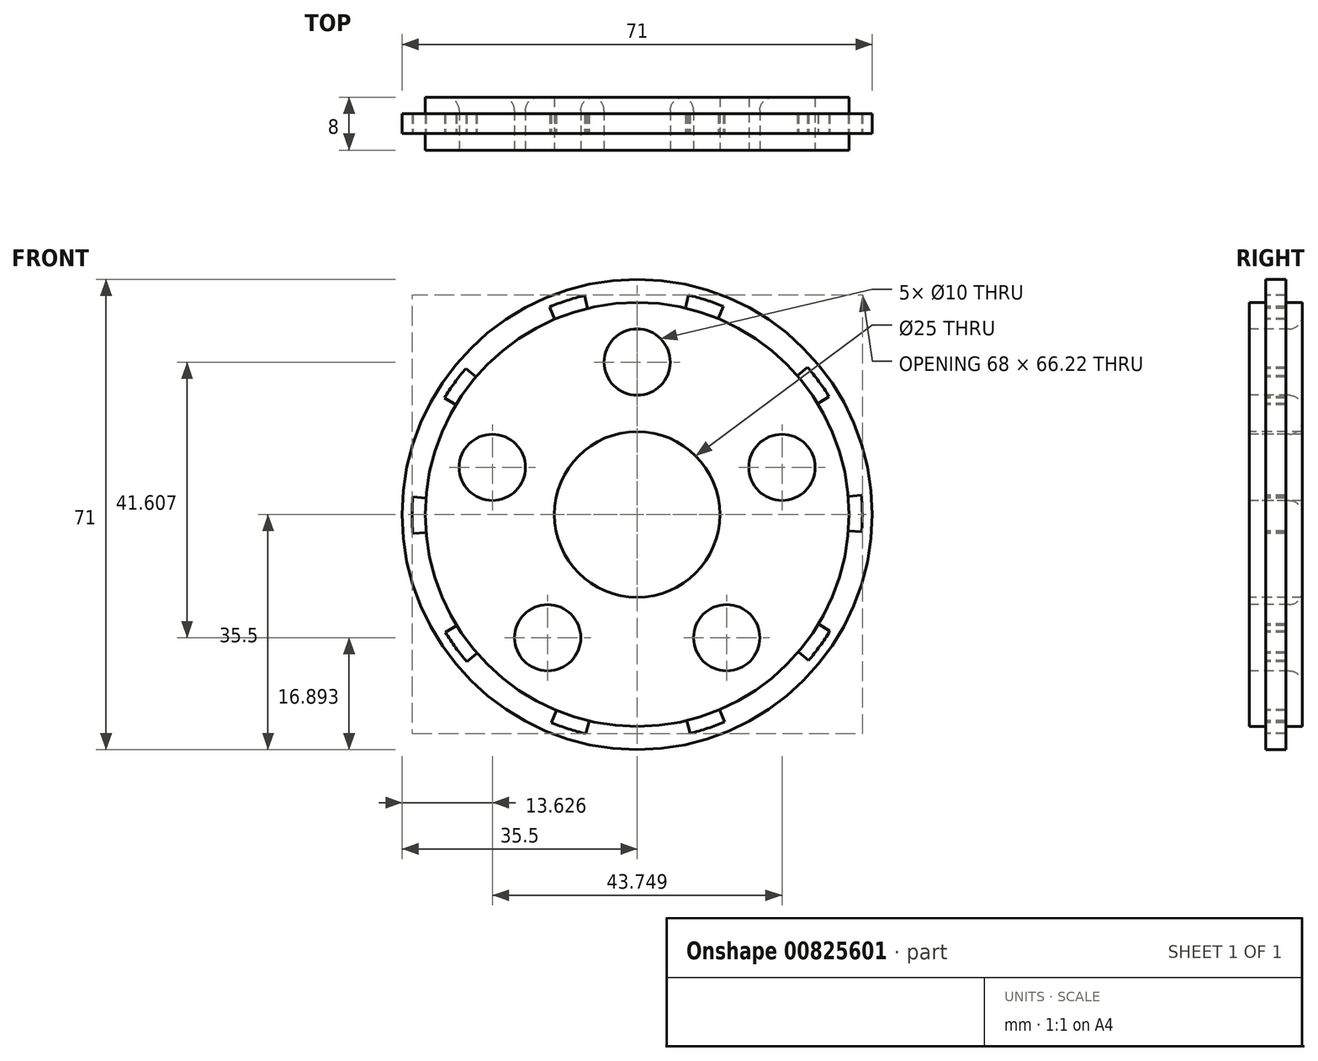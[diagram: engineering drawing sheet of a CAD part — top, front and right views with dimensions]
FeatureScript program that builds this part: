
annotation { "Feature Type Name" : "Feature", "Feature Type Description" : "" }
export const myFeature = defineFeature(function(context is Context, id is Id, definition is map)
    precondition{}
    {
        {
            var Q0;
            Q0=qCreatedBy(makeId("Front.planeOp"),FACE);
            var sketch = newSketch(context, id + "F0", { "sketchPlane" : qUnion([Q0])});
            skCircle(sketch, "E0", {"center": v(0, 0) * mm, "radius": 35.5 * mm});
            skSolve(sketch);
        }
        {
            var Q0;
            Q0=qSketchRegion(id+"F0",true);
            extrude(context, id + "F1", {"entities" : qUnion([Q0]), "oppositeDirection" : true, "depth" : 4 * mm, "hasSecondDirection" : true, "secondDirectionOppositeDirection" : false, "secondDirectionDepth" : 4 * mm, "offsetDistance" : 25 * mm});
        }
        {
            var Q0;
            Q0=makeQuery(id+"F1.opExtrude","CAP_FACE",FACE,{"disambiguationData":[OSD([sQuery(id+"F0.wireOp",EDGE,"E0")])],"isStart":true});
            var sketch = newSketch(context, id + "F2", { "sketchPlane" : qUnion([Q0])});
            skCircle(sketch, "E1", {"center": v(0, 0) * mm, "radius": 12.5 * mm});
            skSolve(sketch);
        }
        {
            var Q0;
            Q0=qSketchRegion(id+"F2",true);
            extrude(context, id + "F3", {"entities" : qUnion([Q0]), "operationType" : NewBodyOperationType.REMOVE, "oppositeDirection" : true, "depth" : 25 * mm});
        }
        {
            var Q0;
            Q0=makeQuery(id+"F1.opExtrude","CAP_FACE",FACE,{"disambiguationData":[OSD([sQuery(id+"F0.wireOp",EDGE,"E0")])],"isStart":true});
            var sketch = newSketch(context, id + "F4", { "sketchPlane" : qUnion([Q0])});
            skCircle(sketch, "E2", {"center": v(0, 23) * mm, "radius": 5 * mm});
            skLineSegment(sketch, "E3", {"start": v(0, 31) * mm, "end": v(0, 15) * mm, "construction": true});
            skCircle(sketch, "E4.1.0", {"center": v(-21.87, 7.1) * mm, "radius": 5 * mm});
            skCircle(sketch, "E4.2.0", {"center": v(-13.52, -18.6) * mm, "radius": 5 * mm});
            skPoint(sketch, "E4.center", {"position": v(0, 0) * mm});
            skCircle(sketch, "E5", {"center": v(0, 0) * mm, "radius": 15 * mm, "construction": true});
            skCircle(sketch, "E6", {"center": v(0, 0) * mm, "radius": 31 * mm, "construction": true});
            skCircle(sketch, "E7.1.3.0", {"center": v(13.52, -18.6) * mm, "radius": 5 * mm});
            skCircle(sketch, "E8.1.4.0", {"center": v(21.87, 7.1) * mm, "radius": 5 * mm});
            skSolve(sketch);
        }
        {
            var Q0;
            Q0=qSketchRegion(id+"F4",true);
            extrude(context, id + "F5", {"entities" : qUnion([Q0]), "operationType" : NewBodyOperationType.REMOVE, "oppositeDirection" : true, "depth" : 25 * mm});
        }
        {
            var Q0;
            Q0=makeQuery(id+"F1.opExtrude","CAP_FACE",FACE,{"disambiguationData":[OSD([sQuery(id+"F0.wireOp",EDGE,"E0")])],"isStart":true});
            var sketch = newSketch(context, id + "F6", { "sketchPlane" : qUnion([Q0])});
            skCircle(sketch, "E9", {"center": v(0, 0) * mm, "radius": 15 * mm, "construction": true});
            skSolve(sketch);
        }
        {
            var Q0;
            Q0=makeQuery(id+"F5.boolean.opBoolean","COPY",EDGE,{"derivedFrom":makeQuery(id+"F5.opExtrude","CAP_EDGE",EDGE,{"disambiguationData":[OSD([sQuery(id+"F4.wireOp",EDGE,"E2")])],"isStart":true})});
            var Q1;
            Q1=makeQuery(id+"F5.boolean.opBoolean","COPY",EDGE,{"derivedFrom":makeQuery(id+"F5.opExtrude","CAP_EDGE",EDGE,{"disambiguationData":[OSD([sQuery(id+"F4.wireOp",EDGE,"E4.1.0")])],"isStart":true})});
            var Q2;
            Q2=makeQuery(id+"F5.boolean.opBoolean","COPY",EDGE,{"derivedFrom":makeQuery(id+"F5.opExtrude","CAP_EDGE",EDGE,{"disambiguationData":[OSD([sQuery(id+"F4.wireOp",EDGE,"E4.2.0")])],"isStart":true})});
            var Q3;
            Q3=makeQuery(id+"F5.boolean.opBoolean","INTERSECT",EDGE,{"derivedFrom":[makeQuery(id+"F1.opExtrude","CAP_FACE",FACE,{"disambiguationData":[OSD([sQuery(id+"F0.wireOp",EDGE,"E0")])],"isStart":false}),makeQuery(id+"F5.opExtrude","SWEPT_FACE",FACE,{"disambiguationData":[OSD([sQuery(id+"F4.wireOp",EDGE,"E4.1.0")])]})]});
            var Q4;
            Q4=makeQuery(id+"F5.boolean.opBoolean","INTERSECT",EDGE,{"derivedFrom":[makeQuery(id+"F1.opExtrude","CAP_FACE",FACE,{"disambiguationData":[OSD([sQuery(id+"F0.wireOp",EDGE,"E0")])],"isStart":false}),makeQuery(id+"F5.opExtrude","SWEPT_FACE",FACE,{"disambiguationData":[OSD([sQuery(id+"F4.wireOp",EDGE,"E4.2.0")])]})]});
            var Q5;
            Q5=makeQuery(id+"F5.boolean.opBoolean","INTERSECT",EDGE,{"derivedFrom":[makeQuery(id+"F1.opExtrude","CAP_FACE",FACE,{"disambiguationData":[OSD([sQuery(id+"F0.wireOp",EDGE,"E0")])],"isStart":false}),makeQuery(id+"F5.opExtrude","SWEPT_FACE",FACE,{"disambiguationData":[OSD([sQuery(id+"F4.wireOp",EDGE,"E2")])]})]});
            var Q6;
            Q6=makeQuery(id+"F5.boolean.opBoolean","COPY",EDGE,{"derivedFrom":makeQuery(id+"F5.opExtrude","CAP_EDGE",EDGE,{"disambiguationData":[OSD([sQuery(id+"F4.wireOp",EDGE,"a81bae41-d5ea-4544-bfaf-6c99a52da0b9.1.5.0")])],"isStart":true})});
            var Q7;
            Q7=makeQuery(id+"F5.boolean.opBoolean","COPY",EDGE,{"derivedFrom":makeQuery(id+"F5.opExtrude","CAP_EDGE",EDGE,{"disambiguationData":[OSD([sQuery(id+"F4.wireOp",EDGE,"E7.1.4.0")])],"isStart":true})});
            var Q8;
            Q8=makeQuery(id+"F5.boolean.opBoolean","COPY",EDGE,{"derivedFrom":makeQuery(id+"F5.opExtrude","CAP_EDGE",EDGE,{"disambiguationData":[OSD([sQuery(id+"F4.wireOp",EDGE,"E7.1.3.0")])],"isStart":true})});
            var Q9;
            Q9=makeQuery(id+"F5.boolean.opBoolean","INTERSECT",EDGE,{"derivedFrom":[makeQuery(id+"F1.opExtrude","CAP_FACE",FACE,{"disambiguationData":[OSD([sQuery(id+"F0.wireOp",EDGE,"E0")])],"isStart":false}),makeQuery(id+"F5.opExtrude","SWEPT_FACE",FACE,{"disambiguationData":[OSD([sQuery(id+"F4.wireOp",EDGE,"E7.1.3.0")])]})]});
            var Q10;
            Q10=makeQuery(id+"F5.boolean.opBoolean","INTERSECT",EDGE,{"derivedFrom":[makeQuery(id+"F1.opExtrude","CAP_FACE",FACE,{"disambiguationData":[OSD([sQuery(id+"F0.wireOp",EDGE,"E0")])],"isStart":false}),makeQuery(id+"F5.opExtrude","SWEPT_FACE",FACE,{"disambiguationData":[OSD([sQuery(id+"F4.wireOp",EDGE,"E7.1.4.0")])]})]});
            var Q11;
            Q11=makeQuery(id+"F5.boolean.opBoolean","INTERSECT",EDGE,{"derivedFrom":[makeQuery(id+"F1.opExtrude","CAP_FACE",FACE,{"disambiguationData":[OSD([sQuery(id+"F0.wireOp",EDGE,"E0")])],"isStart":false}),makeQuery(id+"F5.opExtrude","SWEPT_FACE",FACE,{"disambiguationData":[OSD([sQuery(id+"F4.wireOp",EDGE,"a81bae41-d5ea-4544-bfaf-6c99a52da0b9.1.5.0")])]})]});
            var Q12;
            Q12=makeQuery(id+"F5.boolean.opBoolean","COPY",EDGE,{"derivedFrom":makeQuery(id+"F5.opExtrude","CAP_EDGE",EDGE,{"disambiguationData":[OSD([sQuery(id+"F4.wireOp",EDGE,"E8.1.4.0")])],"isStart":true})});
            fillet(context, id + "F7", {"entities" : qUnion([Q0, Q1, Q2, Q3, Q4, Q5, Q6, Q7, Q8, Q9, Q10, Q11, Q12]), "radius" : 2 * mm, "tangentPropagation" : true, "allowEdgeOverflow" : false});
        }
        {
            var Q0;
            Q0=makeQuery(id+"F6.imprint","IMPRINT",FACE,{"disambiguationData":[TD([[makeQuery(id+"F6.imprint","IMPRINT",EDGE,{"derivedFrom":makeQuery(id+"F1.opExtrude","CAP_EDGE",EDGE,{"disambiguationData":[OSD([sQuery(id+"F0.wireOp",EDGE,"E0")])],"isStart":true})}),1.0]])]});
            var sketch = newSketch(context, id + "F8", { "sketchPlane" : qUnion([Q0])});
            skCircle(sketch, "E10", {"center": v(0, 0) * mm, "radius": 32 * mm});
            skCircle(sketch, "E11", {"center": v(0, 0) * mm, "radius": 36.35 * mm});
            skSolve(sketch);
        }
        {
            var Q0;
            Q0=qSketchRegion(id+"F8",true);
            extrude(context, id + "F9", {"entities" : qUnion([Q0]), "operationType" : NewBodyOperationType.REMOVE, "oppositeDirection" : true, "depth" : 2.5 * mm, "offsetDistance" : 25 * mm});
        }
        {
            var Q0;
            Q0=makeQuery(id+"F1.opExtrude","CAP_FACE",FACE,{"disambiguationData":[OSD([sQuery(id+"F0.wireOp",EDGE,"E0")])],"isStart":false});
            var sketch = newSketch(context, id + "F10", { "sketchPlane" : qUnion([Q0])});
            skCircle(sketch, "E12", {"center": v(0, 0) * mm, "radius": 32 * mm});
            skCircle(sketch, "E13", {"center": v(0, 0) * mm, "radius": 42.23 * mm});
            skSolve(sketch);
        }
        {
            var Q0;
            Q0=qSketchRegion(id+"F10",true);
            extrude(context, id + "F11", {"entities" : qUnion([Q0]), "operationType" : NewBodyOperationType.REMOVE, "oppositeDirection" : true, "depth" : 2.5 * mm, "offsetDistance" : 25 * mm});
        }
        {
            var Q0;
            Q0=makeQuery(id+"F9.boolean.opBoolean","COPY",FACE,{"derivedFrom":makeQuery(id+"F9.opExtrude","CAP_FACE",FACE,{"disambiguationData":[OSD([sQuery(id+"F8.wireOp",EDGE,"E10"),sQuery(id+"F8.wireOp",EDGE,"E11")])],"isStart":false})});
            var sketch = newSketch(context, id + "F12", { "sketchPlane" : qUnion([Q0])});
            skLineSegment(sketch, "E14", {"start": v(0, 33) * mm, "end": v(0, 0) * mm, "construction": true});
            skPoint(sketch, "E15.center", {"position": v(0, 0) * mm});
            skLineSegment(sketch, "E16", {"start": v(0, 0) * mm, "end": v(10.2, 31.38) * mm, "construction": true});
            skArc(sketch, "E17", {"start": v(12.22, 29.58) * mm, "mid": v(9.78, 30.47) * mm, "end": v(7.27, 31.16) * mm});
            skLineSegment(sketch, "E18", {"start": v(7.27, 31.16) * mm, "end": v(0, 0) * mm, "construction": true});
            skLineSegment(sketch, "E19", {"start": v(0, 0) * mm, "end": v(12.22, 29.58) * mm, "construction": true});
            skLineSegment(sketch, "E20", {"start": v(7.27, 31.16) * mm, "end": v(7.73, 33.11) * mm});
            skLineSegment(sketch, "E21", {"start": v(12.22, 29.58) * mm, "end": v(12.98, 31.42) * mm});
            skArc(sketch, "E22", {"start": v(12.98, 31.42) * mm, "mid": v(10.39, 32.37) * mm, "end": v(7.73, 33.11) * mm});
            skArc(sketch, "E23.1.0", {"start": v(-7.97, 33.05) * mm, "mid": v(-10.63, 32.3) * mm, "end": v(-13.21, 31.33) * mm});
            skLineSegment(sketch, "E23.1.1", {"start": v(-12.43, 29.49) * mm, "end": v(-13.21, 31.33) * mm});
            skArc(sketch, "E23.1.2", {"start": v(-7.5, 31.1) * mm, "mid": v(-10, 30.4) * mm, "end": v(-12.43, 29.49) * mm});
            skLineSegment(sketch, "E23.1.3", {"start": v(-7.5, 31.1) * mm, "end": v(-7.97, 33.05) * mm});
            skArc(sketch, "E23.2.0", {"start": v(-25.87, 22.06) * mm, "mid": v(-27.58, 19.88) * mm, "end": v(-29.1, 17.58) * mm});
            skLineSegment(sketch, "E23.2.1", {"start": v(-27.4, 16.55) * mm, "end": v(-29.1, 17.58) * mm});
            skArc(sketch, "E23.2.2", {"start": v(-24.35, 20.76) * mm, "mid": v(-25.96, 18.71) * mm, "end": v(-27.4, 16.55) * mm});
            skLineSegment(sketch, "E23.2.3", {"start": v(-24.35, 20.76) * mm, "end": v(-25.87, 22.06) * mm});
            skArc(sketch, "E23.3.0", {"start": v(-33.9, 2.64) * mm, "mid": v(-34, -0.12) * mm, "end": v(-33.88, -2.88) * mm});
            skLineSegment(sketch, "E23.3.1", {"start": v(-31.88, -2.71) * mm, "end": v(-33.88, -2.88) * mm});
            skArc(sketch, "E23.3.2", {"start": v(-31.9, 2.48) * mm, "mid": v(-32, -0.12) * mm, "end": v(-31.88, -2.71) * mm});
            skLineSegment(sketch, "E23.3.3", {"start": v(-31.9, 2.48) * mm, "end": v(-33.9, 2.64) * mm});
            skArc(sketch, "E23.4.0", {"start": v(-28.97, -17.8) * mm, "mid": v(-27.43, -20.09) * mm, "end": v(-25.71, -22.25) * mm});
            skLineSegment(sketch, "E23.4.1", {"start": v(-24.2, -20.94) * mm, "end": v(-25.71, -22.25) * mm});
            skArc(sketch, "E23.4.2", {"start": v(-27.27, -16.75) * mm, "mid": v(-25.82, -18.9) * mm, "end": v(-24.2, -20.94) * mm});
            skLineSegment(sketch, "E23.4.3", {"start": v(-27.27, -16.75) * mm, "end": v(-28.97, -17.8) * mm});
            skArc(sketch, "E23.5.0", {"start": v(-12.98, -31.42) * mm, "mid": v(-10.39, -32.37) * mm, "end": v(-7.73, -33.11) * mm});
            skLineSegment(sketch, "E23.5.1", {"start": v(-7.27, -31.16) * mm, "end": v(-7.73, -33.11) * mm});
            skArc(sketch, "E23.5.2", {"start": v(-12.22, -29.58) * mm, "mid": v(-9.78, -30.47) * mm, "end": v(-7.27, -31.16) * mm});
            skLineSegment(sketch, "E23.5.3", {"start": v(-12.22, -29.58) * mm, "end": v(-12.98, -31.42) * mm});
            skArc(sketch, "E23.6.0", {"start": v(7.97, -33.05) * mm, "mid": v(10.63, -32.3) * mm, "end": v(13.21, -31.33) * mm});
            skLineSegment(sketch, "E23.6.1", {"start": v(12.43, -29.49) * mm, "end": v(13.21, -31.33) * mm});
            skArc(sketch, "E23.6.2", {"start": v(7.5, -31.1) * mm, "mid": v(10, -30.4) * mm, "end": v(12.43, -29.49) * mm});
            skLineSegment(sketch, "E23.6.3", {"start": v(7.5, -31.1) * mm, "end": v(7.97, -33.05) * mm});
            skArc(sketch, "E23.7.0", {"start": v(25.87, -22.06) * mm, "mid": v(27.58, -19.88) * mm, "end": v(29.1, -17.58) * mm});
            skLineSegment(sketch, "E23.7.1", {"start": v(27.4, -16.55) * mm, "end": v(29.1, -17.58) * mm});
            skArc(sketch, "E23.7.2", {"start": v(24.35, -20.76) * mm, "mid": v(25.96, -18.71) * mm, "end": v(27.4, -16.55) * mm});
            skLineSegment(sketch, "E23.7.3", {"start": v(24.35, -20.76) * mm, "end": v(25.87, -22.06) * mm});
            skArc(sketch, "E23.8.0", {"start": v(33.9, -2.64) * mm, "mid": v(34, 0.12) * mm, "end": v(33.88, 2.88) * mm});
            skLineSegment(sketch, "E23.8.1", {"start": v(31.88, 2.71) * mm, "end": v(33.88, 2.88) * mm});
            skArc(sketch, "E23.8.2", {"start": v(31.9, -2.48) * mm, "mid": v(32, 0.12) * mm, "end": v(31.88, 2.71) * mm});
            skLineSegment(sketch, "E23.8.3", {"start": v(31.9, -2.48) * mm, "end": v(33.9, -2.64) * mm});
            skArc(sketch, "E23.9.0", {"start": v(28.97, 17.8) * mm, "mid": v(27.43, 20.09) * mm, "end": v(25.71, 22.25) * mm});
            skLineSegment(sketch, "E23.9.1", {"start": v(24.2, 20.94) * mm, "end": v(25.71, 22.25) * mm});
            skArc(sketch, "E23.9.2", {"start": v(27.27, 16.75) * mm, "mid": v(25.82, 18.9) * mm, "end": v(24.2, 20.94) * mm});
            skLineSegment(sketch, "E23.9.3", {"start": v(27.27, 16.75) * mm, "end": v(28.97, 17.8) * mm});
            skSolve(sketch);
        }
        {
            var Q0;
            Q0 = qSketchRegion(id + "F12", true);
            extrude(context, id + "F13", {"entities" : qUnion([Q0]), "operationType" : NewBodyOperationType.REMOVE, "oppositeDirection" : true, "depth" : 25 * mm, "offsetDistance" : 25 * mm});
        }
    });
